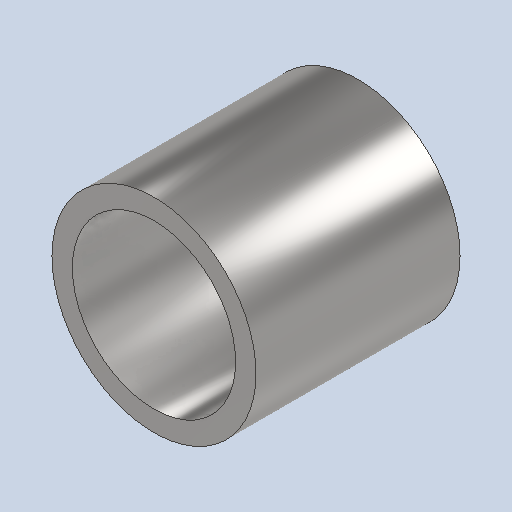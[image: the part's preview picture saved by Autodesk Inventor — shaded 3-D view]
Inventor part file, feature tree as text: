
AUTODESK INVENTOR PART (.ipt)
format: ipt  version: 2022.2 (Build 262287010, 287A)  size: 140,800 bytes
history: native  units: mm
features: extrude x1, sketch x1
ambient origin geometry x8: Origin, YZ Plane, XZ Plane, XY Plane, X Axis, Y Axis, Z Axis, Center Point
bodies: Solid1 (feature_tree)
feature tree (2):
  extrude  "Extrusion1"  Depth=10.0mm
  sketch  "Sketch1"  dims[d0=10.0mm d1=8.0mm d2=10.0mm d3=0.0mm]
